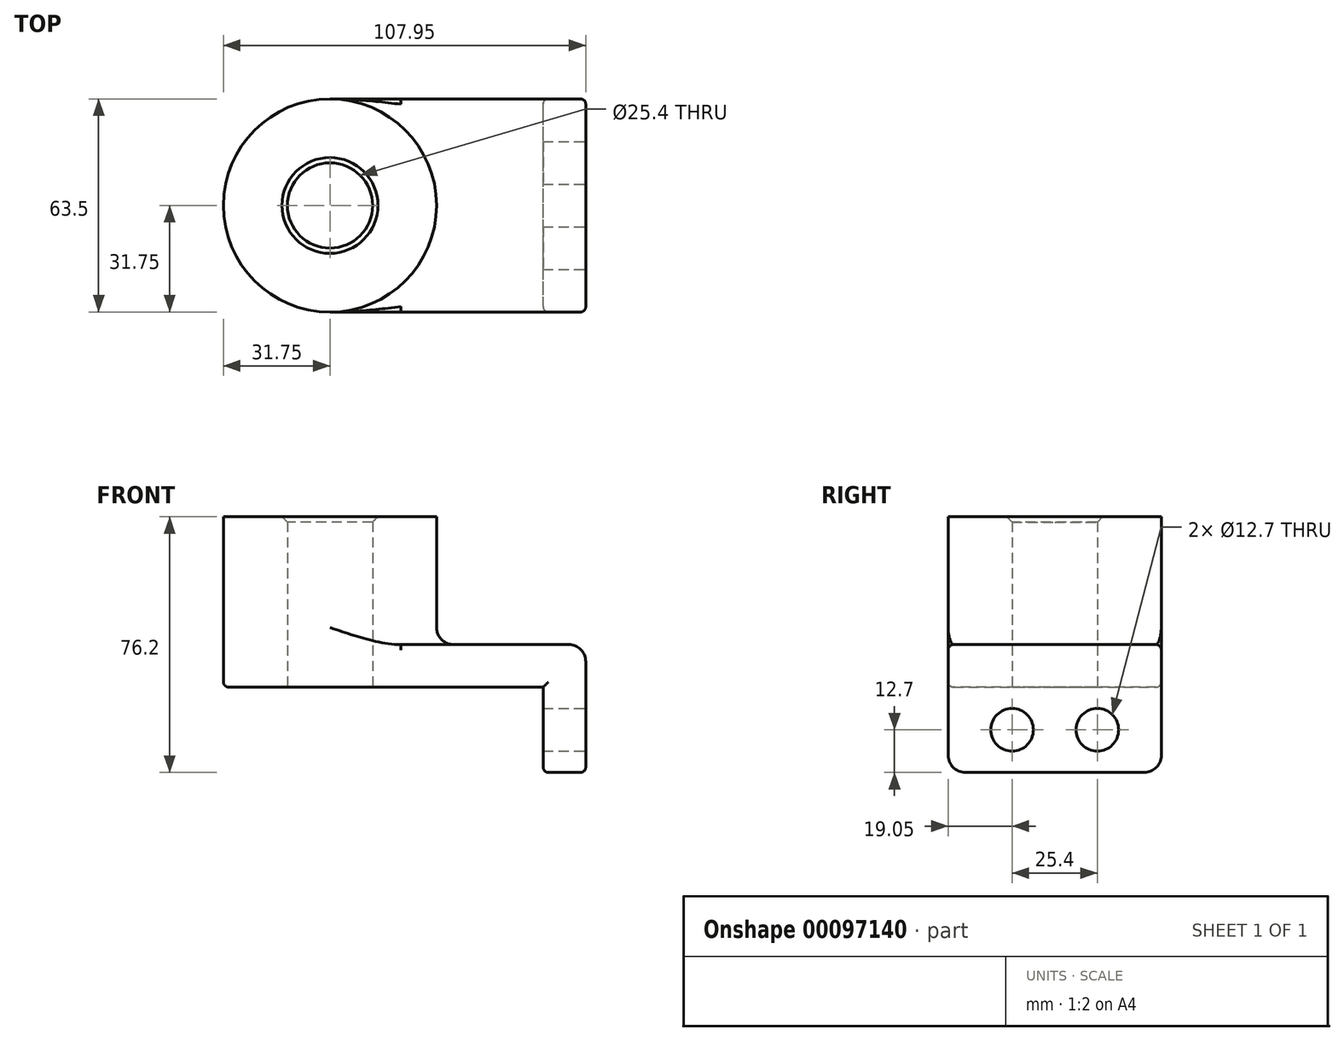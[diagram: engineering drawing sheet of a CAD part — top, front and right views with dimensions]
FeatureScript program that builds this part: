
annotation { "Feature Type Name" : "Feature", "Feature Type Description" : "" }
export const myFeature = defineFeature(function(context is Context, id is Id, definition is map)
    precondition{}
    {
        {
            var Q0;
            Q0=qCreatedBy(makeId("Top.planeOp"),FACE);
            var sketch = newSketch(context, id + "F0", { "sketchPlane" : qUnion([Q0])});
            skLineSegment(sketch, "E0.bottom", {"start": v(38.1, -31.75) * mm, "end": v(-38.1, -31.75) * mm});
            skLineSegment(sketch, "E0.top", {"start": v(38.1, 31.75) * mm, "end": v(-38.1, 31.75) * mm});
            skLineSegment(sketch, "E0.left", {"start": v(38.1, -31.75) * mm, "end": v(38.1, 31.75) * mm});
            skLineSegment(sketch, "E0.right", {"start": v(-38.1, -31.75) * mm, "end": v(-38.1, 31.75) * mm});
            skPoint(sketch, "E0.middle", {"position": v(0, 0) * mm});
            skCircle(sketch, "E1", {"center": v(-38.1, 0) * mm, "radius": 31.75 * mm});
            skCircle(sketch, "E2", {"center": v(-38.1, 0) * mm, "radius": 12.7 * mm});
            skSolve(sketch);
        }
        {
            var Q0;
            {var subQ1=sQuery(id+"F0.wireOp",EDGE,"E0.right");var subQ3=sQuery(id+"F0.wireOp",EDGE,"E2");var subQ4=makeQuery(id+"F0.imprint","INTERSECT",VERTEX,{"disambiguationData":[OD(0.0)],"derivedFrom":[subQ1,subQ3]});Q0=makeQuery(id+"F0.imprint","IMPRINT",FACE,{"disambiguationData":[TD([[makeQuery(id+"F0.imprint","IMPRINT",EDGE,{"disambiguationData":[TD([[subQ4,1.0]])],"derivedFrom":subQ3}),-1.0]])]});}
            var Q1;
            {var subQ1=sQuery(id+"F0.wireOp",EDGE,"E0.right");var subQ3=sQuery(id+"F0.wireOp",EDGE,"E2");var subQ4=makeQuery(id+"F0.imprint","INTERSECT",VERTEX,{"disambiguationData":[OD(0.0)],"derivedFrom":[subQ1,subQ3]});Q1=makeQuery(id+"F0.imprint","IMPRINT",FACE,{"disambiguationData":[TD([[makeQuery(id+"F0.imprint","IMPRINT",EDGE,{"disambiguationData":[TD([[subQ4,-1.0]])],"derivedFrom":subQ3}),-1.0]])]});}
            var Q2;
            {var subQ0=sQuery(id+"F0.wireOp",EDGE,"E0.bottom");Q2=makeQuery(id+"F0.imprint","IMPRINT",FACE,{"disambiguationData":[TD([[makeQuery(id+"F0.imprint","IMPRINT",EDGE,{"derivedFrom":subQ0}),-1.0]])]});}
            extrude(context, id + "F1", {"entities" : qUnion([Q0, Q1, Q2]), "depth" : 12.7 * mm});
        }
        {
            var Q0;
            {var subQ1=sQuery(id+"F0.wireOp",EDGE,"E0.right");var subQ3=sQuery(id+"F0.wireOp",EDGE,"E2");var subQ4=makeQuery(id+"F0.imprint","INTERSECT",VERTEX,{"disambiguationData":[OD(0.0)],"derivedFrom":[subQ1,subQ3]});Q0=makeQuery(id+"F0.imprint","IMPRINT",FACE,{"disambiguationData":[TD([[makeQuery(id+"F0.imprint","IMPRINT",EDGE,{"disambiguationData":[TD([[subQ4,1.0]])],"derivedFrom":subQ3}),-1.0]])]});}
            var Q1;
            {var subQ1=sQuery(id+"F0.wireOp",EDGE,"E0.right");var subQ3=sQuery(id+"F0.wireOp",EDGE,"E2");var subQ4=makeQuery(id+"F0.imprint","INTERSECT",VERTEX,{"disambiguationData":[OD(0.0)],"derivedFrom":[subQ1,subQ3]});Q1=makeQuery(id+"F0.imprint","IMPRINT",FACE,{"disambiguationData":[TD([[makeQuery(id+"F0.imprint","IMPRINT",EDGE,{"disambiguationData":[TD([[subQ4,-1.0]])],"derivedFrom":subQ3}),-1.0]])]});}
            extrude(context, id + "F2", {"entities" : qUnion([Q0, Q1]), "operationType" : NewBodyOperationType.ADD, "depth" : 50.8 * mm});
        }
        {
            var Q0;
            Q0=makeQuery(id+"F1.opExtrude","SWEPT_FACE",FACE,{"disambiguationData":[OSD([sQuery(id+"F0.wireOp",EDGE,"E0.left")])]});
            var sketch = newSketch(context, id + "F3", { "sketchPlane" : qUnion([Q0])});
            skLineSegment(sketch, "E3.bottom", {"start": v(-31.75, 12.7) * mm, "end": v(31.75, 12.7) * mm});
            skLineSegment(sketch, "E3.top", {"start": v(-31.75, -25.4) * mm, "end": v(31.75, -25.4) * mm});
            skLineSegment(sketch, "E3.left", {"start": v(-31.75, 12.7) * mm, "end": v(-31.75, -25.4) * mm});
            skLineSegment(sketch, "E3.right", {"start": v(31.75, 12.7) * mm, "end": v(31.75, -25.4) * mm});
            skCircle(sketch, "E4", {"center": v(-12.7, -12.7) * mm, "radius": 6.35 * mm});
            skLineSegment(sketch, "E5", {"start": v(0, 0) * mm, "end": v(0, -25.4) * mm, "construction": true});
            skCircle(sketch, "E6.MirrorC", {"center": v(12.7, -12.7) * mm, "radius": 6.35 * mm});
            skSolve(sketch);
        }
        {
            var Q0;
            {var subQ2=sQuery(id+"F3.wireOp",EDGE,"E3.top");Q0=makeQuery(id+"F3.imprint","IMPRINT",FACE,{"disambiguationData":[TD([[makeQuery(id+"F3.imprint","IMPRINT",EDGE,{"derivedFrom":subQ2}),1.0]])]});}
            extrude(context, id + "F4", {"entities" : qUnion([Q0]), "operationType" : NewBodyOperationType.ADD, "oppositeDirection" : true, "depth" : 12.7 * mm});
        }
        {
            var Q0;
            {var subQ0=sQuery(id+"F0.wireOp",EDGE,"E1");Q0=makeQuery(id+"F2.boolean.opBoolean","INTERSECT",EDGE,{"derivedFrom":[makeQuery(id+"F1.opExtrude","CAP_FACE",FACE,{"disambiguationData":[OSD([sQuery(id+"F0.wireOp",EDGE,"E0.bottom"),sQuery(id+"F0.wireOp",EDGE,"E0.top"),sQuery(id+"F0.wireOp",EDGE,"E0.left"),subQ0,sQuery(id+"F0.wireOp",EDGE,"E2")])],"isStart":false}),makeQuery(id+"F2.opExtrude","SWEPT_FACE",FACE,{"disambiguationData":[OSD([subQ0])]})]});}
            var Q1;
            Q1=makeQuery(id+"F1.opExtrude","CAP_EDGE",EDGE,{"disambiguationData":[OSD([sQuery(id+"F0.wireOp",EDGE,"E0.left")])],"isStart":false});
            var Q2;
            Q2=makeQuery(id+"F4.opExtrude","SWEPT_EDGE",EDGE,{"disambiguationData":[OSD([sQuery(id+"F3.wireOp",EDGE,"E3.top"),sQuery(id+"F3.wireOp",EDGE,"E3.left")])]});
            var Q3;
            Q3=makeQuery(id+"F4.opExtrude","SWEPT_EDGE",EDGE,{"disambiguationData":[OSD([sQuery(id+"F3.wireOp",EDGE,"E3.top"),sQuery(id+"F3.wireOp",EDGE,"E3.right")])]});
            fillet(context, id + "F5", {"entities" : qUnion([Q0, Q1, Q2, Q3]), "radius" : 5.08 * mm, "tangentPropagation" : true, "allowEdgeOverflow" : false});
        }
        {
            var Q0;
            Q0=makeQuery(id+"F1.opExtrude","CAP_EDGE",EDGE,{"disambiguationData":[OSD([sQuery(id+"F0.wireOp",EDGE,"E0.bottom")])],"isStart":false});
            var Q1;
            Q1=makeQuery(id+"F1.opExtrude","CAP_EDGE",EDGE,{"disambiguationData":[OSD([sQuery(id+"F0.wireOp",EDGE,"E0.bottom")])],"isStart":true});
            var Q2;
            Q2=makeQuery(id+"F1.opExtrude","CAP_EDGE",EDGE,{"disambiguationData":[OSD([sQuery(id+"F0.wireOp",EDGE,"E0.top")])],"isStart":true});
            var Q3;
            Q3=makeQuery(id+"F1.opExtrude","CAP_EDGE",EDGE,{"disambiguationData":[OSD([sQuery(id+"F0.wireOp",EDGE,"E0.top")])],"isStart":false});
            var Q4;
            Q4=makeQuery(id+"F4.opExtrude","CAP_EDGE",EDGE,{"disambiguationData":[OSD([sQuery(id+"F3.wireOp",EDGE,"E3.right")])],"isStart":true});
            var Q5;
            Q5=makeQuery(id+"F4.opExtrude","CAP_EDGE",EDGE,{"disambiguationData":[OSD([sQuery(id+"F3.wireOp",EDGE,"E3.right")])],"isStart":false});
            var Q6;
            Q6=makeQuery(id+"F4.opExtrude","CAP_EDGE",EDGE,{"disambiguationData":[OSD([sQuery(id+"F3.wireOp",EDGE,"E3.left")])],"isStart":true});
            var Q7;
            Q7=makeQuery(id+"F4.opExtrude","CAP_EDGE",EDGE,{"disambiguationData":[OSD([sQuery(id+"F3.wireOp",EDGE,"E3.left")])],"isStart":false});
            var Q8;
            Q8=makeQuery(id+"F4.opExtrude","CAP_EDGE",EDGE,{"disambiguationData":[OSD([sQuery(id+"F0.wireOp",EDGE,"E0.left")])],"isStart":false});
            fillet(context, id + "F6", {"entities" : qUnion([Q0, Q1, Q2, Q3, Q4, Q5, Q6, Q7, Q8]), "radius" : 1.59 * mm, "tangentPropagation" : true, "allowEdgeOverflow" : false});
        }
        {
            var Q0;
            Q0=makeQuery(id+"F2.opExtrude","CAP_EDGE",EDGE,{"disambiguationData":[OSD([sQuery(id+"F0.wireOp",EDGE,"E2")])],"isStart":false});
            chamfer(context, id + "F7", {"entities" : qUnion([Q0]), "width" : 1.59 * mm, "tangentPropagation" : true});
        }
    });
